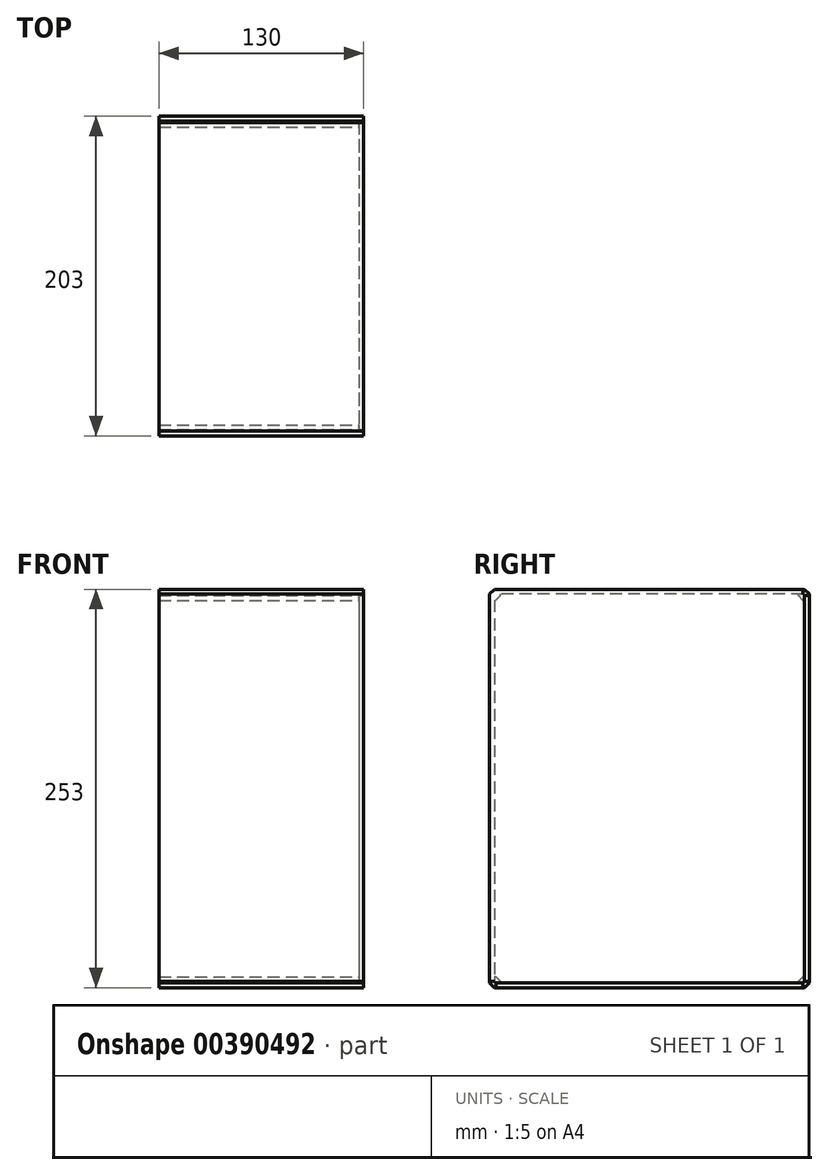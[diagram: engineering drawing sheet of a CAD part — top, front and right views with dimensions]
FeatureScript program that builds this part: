
annotation { "Feature Type Name" : "Feature", "Feature Type Description" : "" }
export const myFeature = defineFeature(function(context is Context, id is Id, definition is map)
    precondition{}
    {
        {
            var Q0;
            Q0=qCreatedBy(makeId("Right.planeOp"),FACE);
            var sketch = newSketch(context, id + "F0", { "sketchPlane" : qUnion([Q0])});
            skLineSegment(sketch, "E0.bottom", {"start": v(97.5, 126.5) * mm, "end": v(-97.5, 126.5) * mm});
            skLineSegment(sketch, "E0.top", {"start": v(97.5, 123.5) * mm, "end": v(-97.5, 123.5) * mm});
            skLineSegment(sketch, "E0.left", {"start": v(97.5, 126.5) * mm, "end": v(97.5, 123.5) * mm});
            skLineSegment(sketch, "E0.right", {"start": v(-97.5, 126.5) * mm, "end": v(-97.5, 123.5) * mm});
            skLineSegment(sketch, "E1.bottom", {"start": v(98.5, 122.5) * mm, "end": v(101.5, 122.5) * mm});
            skLineSegment(sketch, "E1.top", {"start": v(98.5, -122.5) * mm, "end": v(101.5, -122.5) * mm});
            skLineSegment(sketch, "E1.left", {"start": v(98.5, 122.5) * mm, "end": v(98.5, -122.5) * mm});
            skLineSegment(sketch, "E1.right", {"start": v(101.5, 122.5) * mm, "end": v(101.5, -122.5) * mm});
            skLineSegment(sketch, "E2", {"start": v(101.5, 122.5) * mm, "end": v(101.5, 123.5) * mm});
            skLineSegment(sketch, "E3", {"start": v(97.5, 126.5) * mm, "end": v(98.5, 126.5) * mm});
            skLineSegment(sketch, "E4", {"start": v(101.5, 123.5) * mm, "end": v(98.5, 126.5) * mm});
            skLineSegment(sketch, "E5", {"start": v(98.5, 119.5) * mm, "end": v(97.5, 119.5) * mm});
            skLineSegment(sketch, "E6", {"start": v(97.5, 119.5) * mm, "end": v(94.5, 122.5) * mm});
            skLineSegment(sketch, "E7", {"start": v(94.5, 122.5) * mm, "end": v(94.5, 123.5) * mm});
            skLineSegment(sketch, "E8", {"start": v(-97.5, 123.5) * mm, "end": v(-98.5, 123.5) * mm});
            skLineSegment(sketch, "E9", {"start": v(-98.5, 123.5) * mm, "end": v(-98.5, 122.5) * mm});
            skLineSegment(sketch, "E10", {"start": v(-97.5, 126.5) * mm, "end": v(-98.5, 126.5) * mm});
            skLineSegment(sketch, "E11", {"start": v(-98.5, 126.5) * mm, "end": v(-101.5, 123.5) * mm});
            skLineSegment(sketch, "E12", {"start": v(-101.5, 123.5) * mm, "end": v(-101.5, 122.5) * mm});
            skLineSegment(sketch, "E13", {"start": v(-98.5, 122.5) * mm, "end": v(-101.5, 122.5) * mm});
            skLineSegment(sketch, "E14", {"start": v(-98.5, 122.5) * mm, "end": v(-98.5, -122.5) * mm});
            skLineSegment(sketch, "E15", {"start": v(-98.5, -122.5) * mm, "end": v(-101.5, -122.5) * mm});
            skLineSegment(sketch, "E16", {"start": v(-101.5, -122.5) * mm, "end": v(-101.5, 122.5) * mm});
            skLineSegment(sketch, "E17", {"start": v(0, 0) * mm, "end": v(-98.5, 0) * mm, "construction": true});
            skLineSegment(sketch, "E18", {"start": v(0, 0) * mm, "end": v(0, 123.5) * mm, "construction": true});
            skLineSegment(sketch, "E19", {"start": v(98.5, -122.5) * mm, "end": v(98.5, -123.5) * mm});
            skLineSegment(sketch, "E20", {"start": v(98.5, -123.5) * mm, "end": v(97.5, -123.5) * mm});
            skLineSegment(sketch, "E21.bottom", {"start": v(97.5, -123.5) * mm, "end": v(-97.5, -123.5) * mm});
            skLineSegment(sketch, "E21.top", {"start": v(97.5, -126.5) * mm, "end": v(-97.5, -126.5) * mm});
            skLineSegment(sketch, "E21.left", {"start": v(97.5, -123.5) * mm, "end": v(97.5, -126.5) * mm});
            skLineSegment(sketch, "E21.right", {"start": v(-97.5, -123.5) * mm, "end": v(-97.5, -126.5) * mm});
            skLineSegment(sketch, "E22", {"start": v(101.5, -122.5) * mm, "end": v(101.5, -123.5) * mm});
            skLineSegment(sketch, "E23", {"start": v(101.5, -123.5) * mm, "end": v(98.5, -126.5) * mm});
            skLineSegment(sketch, "E24", {"start": v(98.5, -126.5) * mm, "end": v(97.5, -126.5) * mm});
            skLineSegment(sketch, "E25", {"start": v(94.5, -123.5) * mm, "end": v(94.5, -122.5) * mm});
            skLineSegment(sketch, "E26", {"start": v(94.5, -122.5) * mm, "end": v(97.5, -119.5) * mm});
            skLineSegment(sketch, "E27", {"start": v(97.5, -119.5) * mm, "end": v(98.5, -119.5) * mm});
            skLineSegment(sketch, "E28", {"start": v(-97.5, -126.5) * mm, "end": v(-98.5, -126.5) * mm});
            skLineSegment(sketch, "E29", {"start": v(-98.5, -126.5) * mm, "end": v(-101.5, -123.5) * mm});
            skLineSegment(sketch, "E30", {"start": v(-101.5, -123.5) * mm, "end": v(-101.5, -122.5) * mm});
            skLineSegment(sketch, "E31", {"start": v(-94.5, -123.5) * mm, "end": v(-94.5, -122.5) * mm});
            skLineSegment(sketch, "E32", {"start": v(-94.5, -122.5) * mm, "end": v(-97.5, -119.5) * mm});
            skLineSegment(sketch, "E33", {"start": v(-97.5, -119.5) * mm, "end": v(-98.5, -119.5) * mm});
            skLineSegment(sketch, "E34.bottom", {"start": v(95.5, 82.5) * mm, "end": v(-74.5, 82.5) * mm, "construction": true});
            skLineSegment(sketch, "E34.top", {"start": v(95.5, -87.5) * mm, "end": v(-74.5, -87.5) * mm, "construction": true});
            skLineSegment(sketch, "E34.left", {"start": v(95.5, 82.5) * mm, "end": v(95.5, -87.5) * mm, "construction": true});
            skLineSegment(sketch, "E34.right", {"start": v(-74.5, 82.5) * mm, "end": v(-74.5, -87.5) * mm, "construction": true});
            skLineSegment(sketch, "E35", {"start": v(95.5, -87.5) * mm, "end": v(98.5, -87.5) * mm, "construction": true});
            skLineSegment(sketch, "E36", {"start": v(97.5, 123.5) * mm, "end": v(98.5, 123.5) * mm});
            skLineSegment(sketch, "E37", {"start": v(98.5, 123.5) * mm, "end": v(98.5, 122.5) * mm});
            skLineSegment(sketch, "E38", {"start": v(-97.5, -123.5) * mm, "end": v(-98.5, -123.5) * mm});
            skLineSegment(sketch, "E39", {"start": v(-98.5, -123.5) * mm, "end": v(-98.5, -122.5) * mm});
            skLineSegment(sketch, "E40", {"start": v(-98.5, 119.5) * mm, "end": v(-97.88, 119.5) * mm});
            skLineSegment(sketch, "E41", {"start": v(-97.88, 119.5) * mm, "end": v(-94.5, 122.5) * mm});
            skLineSegment(sketch, "E42", {"start": v(-94.5, 122.5) * mm, "end": v(-94.5, 123.5) * mm});
            skSolve(sketch);
        }
        {
            var Q0;
            Q0=makeQuery(id+"F0.imprint","IMPRINT",FACE,{"disambiguationData":[TD([[makeQuery(id+"F0.imprint","IMPRINT",EDGE,{"derivedFrom":sQuery(id+"F0.wireOp",EDGE,"E1.top")}),-1.0]])]});
            var Q1;
            {var subQ4=sQuery(id+"F0.wireOp",EDGE,"E19");Q1=makeQuery(id+"F0.imprint","IMPRINT",FACE,{"disambiguationData":[TD([[makeQuery(id+"F0.imprint","IMPRINT",EDGE,{"derivedFrom":subQ4}),-1.0]])]});}
            var Q2;
            Q2=makeQuery(id+"F0.imprint","IMPRINT",FACE,{"disambiguationData":[TD([[makeQuery(id+"F0.imprint","IMPRINT",EDGE,{"derivedFrom":sQuery(id+"F0.wireOp",EDGE,"E0.left")}),1.0]])]});
            var Q3;
            {var subQ0=sQuery(id+"F0.wireOp",EDGE,"E5");Q3=makeQuery(id+"F0.imprint","IMPRINT",FACE,{"disambiguationData":[TD([[makeQuery(id+"F0.imprint","IMPRINT",EDGE,{"derivedFrom":subQ0}),-1.0]])]});}
            var Q4;
            {var subQ3=sQuery(id+"F0.wireOp",EDGE,"E8");Q4=makeQuery(id+"F0.imprint","IMPRINT",FACE,{"disambiguationData":[TD([[makeQuery(id+"F0.imprint","IMPRINT",EDGE,{"derivedFrom":subQ3}),1.0]])]});}
            var Q5;
            Q5=makeQuery(id+"F0.imprint","IMPRINT",FACE,{"disambiguationData":[TD([[makeQuery(id+"F0.imprint","IMPRINT",EDGE,{"derivedFrom":sQuery(id+"F0.wireOp",EDGE,"E0.right")}),-1.0]])]});
            var Q6;
            Q6=makeQuery(id+"F0.imprint","IMPRINT",FACE,{"disambiguationData":[TD([[makeQuery(id+"F0.imprint","IMPRINT",EDGE,{"derivedFrom":sQuery(id+"F0.wireOp",EDGE,"E15")}),1.0]])]});
            var Q7;
            {var subQ2=sQuery(id+"F0.wireOp",EDGE,"E31");Q7=makeQuery(id+"F0.imprint","IMPRINT",FACE,{"disambiguationData":[TD([[makeQuery(id+"F0.imprint","IMPRINT",EDGE,{"derivedFrom":subQ2}),1.0]])]});}
            extrude(context, id + "F1", {"entities" : qUnion([Q0, Q1, Q2, Q3, Q4, Q5, Q6, Q7]), "oppositeDirection" : true, "depth" : 130 * mm});
        }
        {
            var Q0;
            Q0=makeQuery(id+"F0.imprint","IMPRINT",FACE,{"disambiguationData":[TD([[makeQuery(id+"F0.imprint","IMPRINT",EDGE,{"derivedFrom":sQuery(id+"F0.wireOp",EDGE,"E0.bottom")}),1.0]])]});
            var Q1;
            {var subQ3=sQuery(id+"F0.wireOp",EDGE,"E1.bottom");Q1=makeQuery(id+"F0.imprint","IMPRINT",FACE,{"disambiguationData":[TD([[makeQuery(id+"F0.imprint","IMPRINT",EDGE,{"derivedFrom":subQ3}),-1.0]])]});}
            var Q2;
            {var subQ4=sQuery(id+"F0.wireOp",EDGE,"E13");Q2=makeQuery(id+"F0.imprint","IMPRINT",FACE,{"disambiguationData":[TD([[makeQuery(id+"F0.imprint","IMPRINT",EDGE,{"derivedFrom":subQ4}),1.0]])]});}
            var Q3;
            Q3=makeQuery(id+"F0.imprint","IMPRINT",FACE,{"disambiguationData":[TD([[makeQuery(id+"F0.imprint","IMPRINT",EDGE,{"derivedFrom":sQuery(id+"F0.wireOp",EDGE,"E21.top")}),-1.0]])]});
            extrude(context, id + "F2", {"entities" : qUnion([Q0, Q1, Q2, Q3]), "oppositeDirection" : true, "depth" : 130 * mm});
        }
        {
            var Q0;
            {var subQ0=sQuery(id+"F0.wireOp",EDGE,"E5");Q0=makeQuery(id+"F0.imprint","IMPRINT",FACE,{"disambiguationData":[TD([[makeQuery(id+"F0.imprint","IMPRINT",EDGE,{"derivedFrom":subQ0}),-1.0]])]});}
            var Q1;
            {var subQ3=sQuery(id+"F0.wireOp",EDGE,"E8");Q1=makeQuery(id+"F0.imprint","IMPRINT",FACE,{"disambiguationData":[TD([[makeQuery(id+"F0.imprint","IMPRINT",EDGE,{"derivedFrom":subQ3}),1.0]])]});}
            var Q2;
            {var subQ2=sQuery(id+"F0.wireOp",EDGE,"E31");Q2=makeQuery(id+"F0.imprint","IMPRINT",FACE,{"disambiguationData":[TD([[makeQuery(id+"F0.imprint","IMPRINT",EDGE,{"derivedFrom":subQ2}),1.0]])]});}
            var Q3;
            {var subQ4=sQuery(id+"F0.wireOp",EDGE,"E19");Q3=makeQuery(id+"F0.imprint","IMPRINT",FACE,{"disambiguationData":[TD([[makeQuery(id+"F0.imprint","IMPRINT",EDGE,{"derivedFrom":subQ4}),-1.0]])]});}
            extrude(context, id + "F3", {"entities" : qUnion([Q0, Q1, Q2, Q3]), "operationType" : NewBodyOperationType.REMOVE, "oppositeDirection" : true, "depth" : 3 * mm});
        }
        {
            var Q0;
            {var subQ4=sQuery(id+"F0.wireOp",EDGE,"E5");Q0=makeQuery(id+"F0.imprint","IMPRINT",FACE,{"disambiguationData":[TD([[makeQuery(id+"F0.imprint","IMPRINT",EDGE,{"derivedFrom":subQ4}),1.0]])]});}
            var Q1;
            {var subQ0=sQuery(id+"F0.wireOp",EDGE,"E5");Q1=makeQuery(id+"F0.imprint","IMPRINT",FACE,{"disambiguationData":[TD([[makeQuery(id+"F0.imprint","IMPRINT",EDGE,{"derivedFrom":subQ0}),-1.0]])]});}
            var Q2;
            {var subQ3=sQuery(id+"F0.wireOp",EDGE,"E8");Q2=makeQuery(id+"F0.imprint","IMPRINT",FACE,{"disambiguationData":[TD([[makeQuery(id+"F0.imprint","IMPRINT",EDGE,{"derivedFrom":subQ3}),1.0]])]});}
            var Q3;
            {var subQ2=sQuery(id+"F0.wireOp",EDGE,"E31");Q3=makeQuery(id+"F0.imprint","IMPRINT",FACE,{"disambiguationData":[TD([[makeQuery(id+"F0.imprint","IMPRINT",EDGE,{"derivedFrom":subQ2}),1.0]])]});}
            var Q4;
            {var subQ4=sQuery(id+"F0.wireOp",EDGE,"E19");Q4=makeQuery(id+"F0.imprint","IMPRINT",FACE,{"disambiguationData":[TD([[makeQuery(id+"F0.imprint","IMPRINT",EDGE,{"derivedFrom":subQ4}),-1.0]])]});}
            extrude(context, id + "F4", {"entities" : qUnion([Q0, Q1, Q2, Q3, Q4]), "oppositeDirection" : true, "depth" : 3 * mm});
        }
        {
            var Q0;
            {var subQ0=sQuery(id+"F0.wireOp",EDGE,"E0.top");Q0=makeQuery(id+"F1.opExtrude","SWEPT_FACE",FACE,{"disambiguationData":[OSD([subQ0]),TDD([makeQuery(id+"F0.imprint","IMPRINT",EDGE,{"disambiguationData":[TD([[makeQuery(id+"F0.imprint","INTERSECT",VERTEX,{"derivedFrom":[subQ0,sQuery(id+"F0.wireOp",EDGE,"E42")]}),-1.0]])],"derivedFrom":subQ0})])]});}
            var sketch = newSketch(context, id + "F5", { "sketchPlane" : qUnion([Q0])});
            skLineSegment(sketch, "E43", {"start": v(-3, -97.5) * mm, "end": v(0, -97.5) * mm});
            skLineSegment(sketch, "E44", {"start": v(0, -97.5) * mm, "end": v(0, -91.5) * mm});
            skLineSegment(sketch, "E45", {"start": v(0, -91.5) * mm, "end": v(-6, -97.5) * mm});
            skLineSegment(sketch, "E46", {"start": v(-6, -97.5) * mm, "end": v(-3, -97.5) * mm});
            skSolve(sketch);
        }
        {
            var Q0;
            {var subQ0=sQuery(id+"F0.wireOp",EDGE,"E14");Q0=makeQuery(id+"F1.opExtrude","SWEPT_FACE",FACE,{"disambiguationData":[OSD([subQ0]),TDD([makeQuery(id+"F0.imprint","IMPRINT",EDGE,{"disambiguationData":[TD([[makeQuery(id+"F0.imprint","INTERSECT",VERTEX,{"derivedFrom":[subQ0,sQuery(id+"F0.wireOp",EDGE,"E40")]}),1.0]])],"derivedFrom":subQ0})])]});}
            var sketch = newSketch(context, id + "F6", { "sketchPlane" : qUnion([Q0])});
            skLineSegment(sketch, "E47", {"start": v(-6, 122.5) * mm, "end": v(0, 116.5) * mm});
            skLineSegment(sketch, "E48", {"start": v(0, 116.5) * mm, "end": v(0, 122.5) * mm});
            skLineSegment(sketch, "E49", {"start": v(0, 122.5) * mm, "end": v(-6, 122.5) * mm});
            skSolve(sketch);
        }
        {
            var Q0;
            Q0 = qSketchRegion(id + "F5", true);
            extrude(context, id + "F7", {"entities" : qUnion([Q0]), "operationType" : NewBodyOperationType.ADD, "depth" : 3 * mm});
        }
        {
            var Q0;
            {var subQ1=sQuery(id+"F0.wireOp",EDGE,"E14");var subQ3=sQuery(id+"F0.wireOp",EDGE,"E9");var subQ4=sQuery(id+"F0.wireOp",EDGE,"E40");var subQ5=makeQuery(id+"F1.opExtrude","SWEPT_FACE",FACE,{"disambiguationData":[OSD([subQ1]),TDD([makeQuery(id+"F0.imprint","IMPRINT",EDGE,{"disambiguationData":[TD([[makeQuery(id+"F0.imprint","INTERSECT",VERTEX,{"derivedFrom":[subQ1,subQ4]}),1.0]])],"derivedFrom":subQ1})])]});var subQ6=makeQuery(id+"F3.boolean.opBoolean","COPY",EDGE,{"disambiguationData":[topologyDisambiguationEdgeConnected([subQ5])],"derivedFrom":makeQuery(id+"F3.opExtrude","CAP_EDGE",EDGE,{"disambiguationData":[OSD([subQ3,subQ1])],"isStart":false})});Q0=makeQuery(id+"F6.imprint","IMPRINT",FACE,{"disambiguationData":[TD([[makeQuery(id+"F6.imprint","IMPRINT",EDGE,{"derivedFrom":subQ6}),-1.0]])]});}
            var Q1;
            {var subQ5=sQuery(id+"F6.wireOp",EDGE,"E48");Q1=makeQuery(id+"F6.imprint","IMPRINT",FACE,{"disambiguationData":[TD([[makeQuery(id+"F6.imprint","IMPRINT",EDGE,{"derivedFrom":subQ5}),1.0]])]});}
            extrude(context, id + "F8", {"entities" : qUnion([Q0, Q1]), "operationType" : NewBodyOperationType.ADD, "depth" : 3 * mm});
        }
    });
